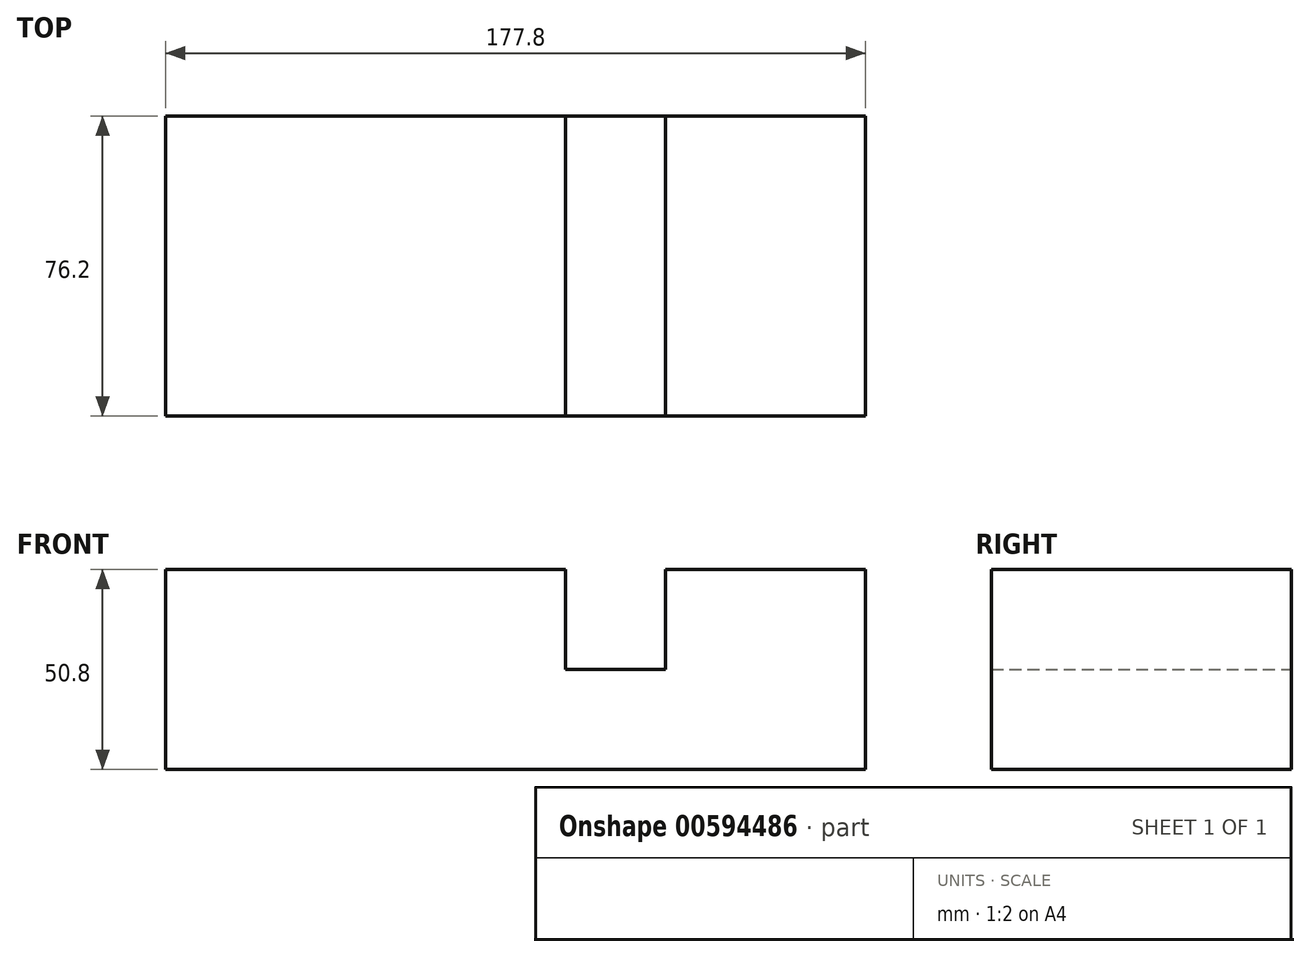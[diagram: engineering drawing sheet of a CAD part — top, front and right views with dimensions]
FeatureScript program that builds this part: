
annotation { "Feature Type Name" : "Feature", "Feature Type Description" : "" }
export const myFeature = defineFeature(function(context is Context, id is Id, definition is map)
    precondition{}
    {
        {
            var Q0;
            Q0=qCreatedBy(makeId("Front.planeOp"),FACE);
            var sketch = newSketch(context, id + "F0", { "sketchPlane" : qUnion([Q0])});
            skLineSegment(sketch, "E0", {"start": v(0, 0) * mm, "end": v(0, 50.8) * mm});
            skLineSegment(sketch, "E1", {"start": v(0, 50.8) * mm, "end": v(101.6, 50.8) * mm});
            skLineSegment(sketch, "E2", {"start": v(101.6, 50.8) * mm, "end": v(101.6, 25.4) * mm});
            skLineSegment(sketch, "E3", {"start": v(101.6, 25.4) * mm, "end": v(127, 25.4) * mm});
            skLineSegment(sketch, "E4", {"start": v(127, 25.4) * mm, "end": v(127, 50.8) * mm});
            skLineSegment(sketch, "E5", {"start": v(127, 50.8) * mm, "end": v(177.8, 50.8) * mm});
            skLineSegment(sketch, "E6", {"start": v(177.8, 50.8) * mm, "end": v(177.8, 0) * mm});
            skLineSegment(sketch, "E7", {"start": v(0, 0) * mm, "end": v(177.8, 0) * mm});
            skSolve(sketch);
        }
        {
            var Q0;
            Q0 = qSketchRegion(id + "F0", true);
            extrude(context, id + "F1", {"entities" : qUnion([Q0]), "depth" : 76.2 * mm, "offsetDistance" : 25.4 * mm});
        }
    });
